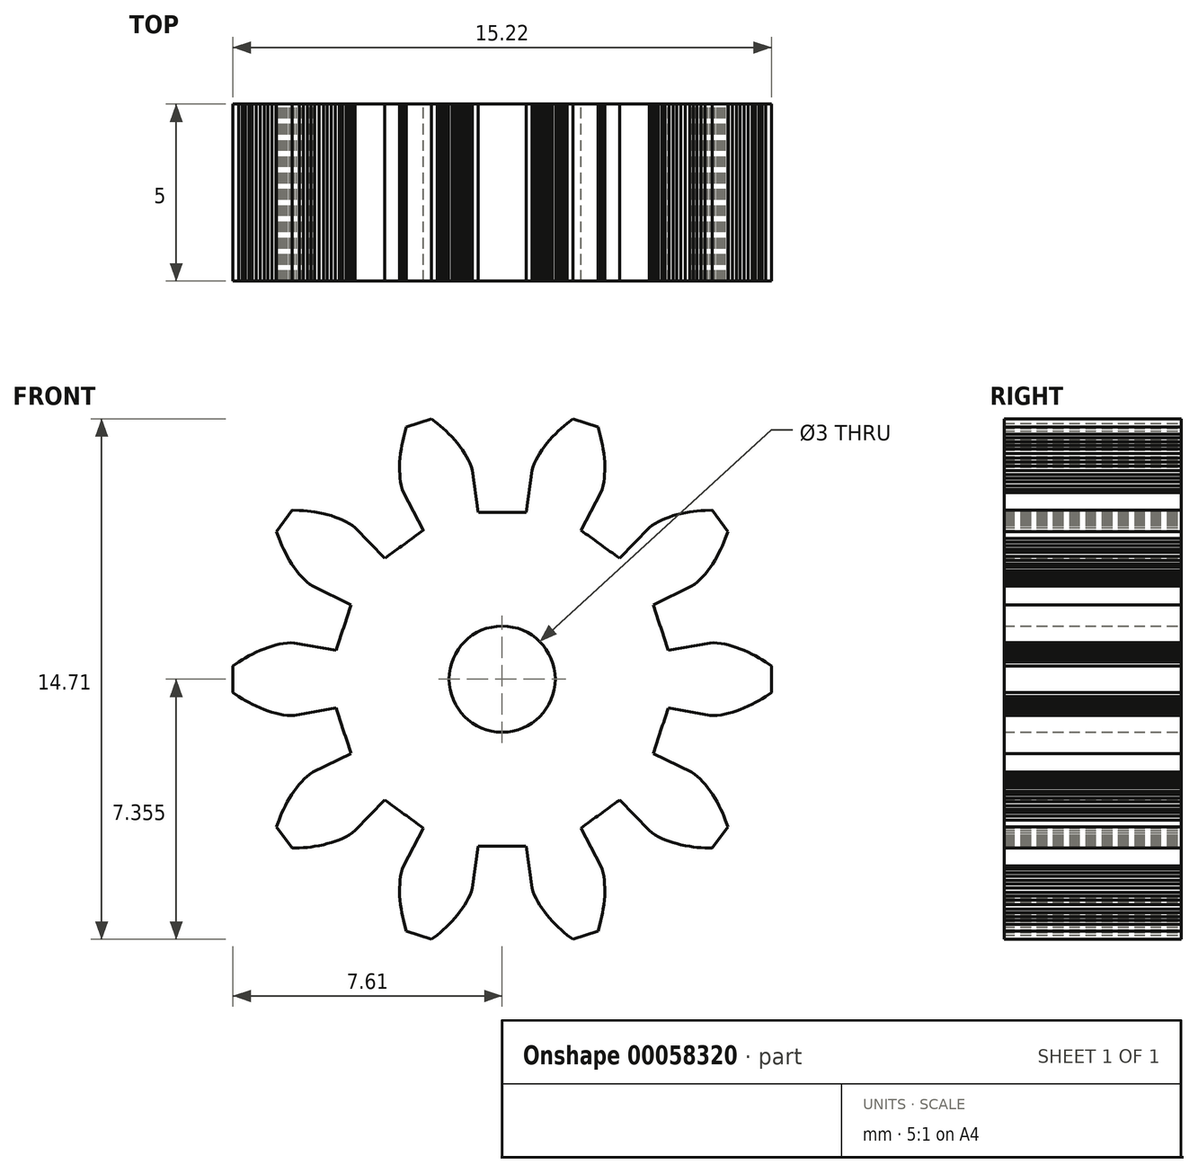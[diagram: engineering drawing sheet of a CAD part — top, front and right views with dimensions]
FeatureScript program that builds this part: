
annotation { "Feature Type Name" : "Feature", "Feature Type Description" : "" }
export const myFeature = defineFeature(function(context is Context, id is Id, definition is map)
    precondition{}
    {
        {
            var Q0;
            Q0=qCreatedBy(makeId("Front.planeOp"),FACE);
            var sketch = newSketch(context, id + "F0", { "sketchPlane" : qUnion([Q0])});
            skLineSegment(sketch, "E0", {"start": v(4.7, 0.36) * mm, "end": v(5.88, 0.15) * mm});
            skLineSegment(sketch, "E1", {"start": v(5.88, 0.15) * mm, "end": v(5.98, 0.15) * mm});
            skLineSegment(sketch, "E2", {"start": v(5.98, 0.15) * mm, "end": v(6.08, 0.15) * mm});
            skLineSegment(sketch, "E3", {"start": v(6.08, 0.15) * mm, "end": v(6.19, 0.17) * mm});
            skLineSegment(sketch, "E4", {"start": v(6.19, 0.17) * mm, "end": v(6.3, 0.19) * mm});
            skLineSegment(sketch, "E5", {"start": v(6.3, 0.19) * mm, "end": v(6.4, 0.2) * mm});
            skLineSegment(sketch, "E6", {"start": v(6.4, 0.2) * mm, "end": v(6.5, 0.24) * mm});
            skLineSegment(sketch, "E7", {"start": v(6.5, 0.24) * mm, "end": v(6.63, 0.28) * mm});
            skLineSegment(sketch, "E8", {"start": v(6.63, 0.28) * mm, "end": v(6.73, 0.32) * mm});
            skLineSegment(sketch, "E9", {"start": v(6.73, 0.32) * mm, "end": v(6.84, 0.36) * mm});
            skLineSegment(sketch, "E10", {"start": v(6.84, 0.36) * mm, "end": v(6.95, 0.4) * mm});
            skLineSegment(sketch, "E11", {"start": v(6.95, 0.4) * mm, "end": v(7.07, 0.47) * mm});
            skLineSegment(sketch, "E12", {"start": v(7.07, 0.47) * mm, "end": v(7.16, 0.52) * mm});
            skLineSegment(sketch, "E13", {"start": v(7.16, 0.52) * mm, "end": v(7.25, 0.57) * mm});
            skLineSegment(sketch, "E14", {"start": v(7.25, 0.57) * mm, "end": v(7.35, 0.63) * mm});
            skLineSegment(sketch, "E15", {"start": v(7.35, 0.63) * mm, "end": v(7.44, 0.69) * mm});
            skLineSegment(sketch, "E16", {"start": v(7.44, 0.69) * mm, "end": v(7.61, 0.8) * mm});
            skLineSegment(sketch, "E17", {"start": v(7.61, 0.8) * mm, "end": v(7.61, 1.55) * mm});
            skLineSegment(sketch, "E18", {"start": v(7.61, 1.55) * mm, "end": v(7.44, 1.66) * mm});
            skLineSegment(sketch, "E19", {"start": v(7.44, 1.66) * mm, "end": v(7.35, 1.72) * mm});
            skLineSegment(sketch, "E20", {"start": v(7.35, 1.72) * mm, "end": v(7.25, 1.78) * mm});
            skLineSegment(sketch, "E21", {"start": v(7.25, 1.78) * mm, "end": v(7.16, 1.83) * mm});
            skLineSegment(sketch, "E22", {"start": v(7.16, 1.83) * mm, "end": v(7.07, 1.88) * mm});
            skLineSegment(sketch, "E23", {"start": v(7.07, 1.88) * mm, "end": v(6.95, 1.94) * mm});
            skLineSegment(sketch, "E24", {"start": v(6.95, 1.94) * mm, "end": v(6.84, 1.99) * mm});
            skLineSegment(sketch, "E25", {"start": v(6.84, 1.99) * mm, "end": v(6.73, 2.03) * mm});
            skLineSegment(sketch, "E26", {"start": v(6.73, 2.03) * mm, "end": v(6.63, 2.07) * mm});
            skLineSegment(sketch, "E27", {"start": v(6.63, 2.07) * mm, "end": v(6.5, 2.1) * mm});
            skLineSegment(sketch, "E28", {"start": v(6.5, 2.1) * mm, "end": v(6.4, 2.14) * mm});
            skLineSegment(sketch, "E29", {"start": v(6.4, 2.14) * mm, "end": v(6.3, 2.16) * mm});
            skLineSegment(sketch, "E30", {"start": v(6.3, 2.16) * mm, "end": v(6.19, 2.18) * mm});
            skLineSegment(sketch, "E31", {"start": v(6.19, 2.18) * mm, "end": v(6.08, 2.2) * mm});
            skLineSegment(sketch, "E32", {"start": v(6.08, 2.2) * mm, "end": v(5.98, 2.2) * mm});
            skLineSegment(sketch, "E33", {"start": v(5.98, 2.2) * mm, "end": v(5.88, 2.2) * mm});
            skLineSegment(sketch, "E34", {"start": v(5.88, 2.2) * mm, "end": v(4.7, 1.99) * mm});
            skArc(sketch, "E35", {"start": v(4.7, 1.99) * mm, "mid": v(4.48, 2.63) * mm, "end": v(4.28, 3.27) * mm});
            skLineSegment(sketch, "E36", {"start": v(4.28, 3.27) * mm, "end": v(5.36, 3.8) * mm});
            skLineSegment(sketch, "E37", {"start": v(5.36, 3.8) * mm, "end": v(5.44, 3.86) * mm});
            skLineSegment(sketch, "E38", {"start": v(5.44, 3.86) * mm, "end": v(5.52, 3.92) * mm});
            skLineSegment(sketch, "E39", {"start": v(5.52, 3.92) * mm, "end": v(5.6, 4) * mm});
            skLineSegment(sketch, "E40", {"start": v(5.6, 4) * mm, "end": v(5.67, 4.08) * mm});
            skLineSegment(sketch, "E41", {"start": v(5.67, 4.08) * mm, "end": v(5.74, 4.15) * mm});
            skLineSegment(sketch, "E42", {"start": v(5.74, 4.15) * mm, "end": v(5.81, 4.24) * mm});
            skLineSegment(sketch, "E43", {"start": v(5.81, 4.24) * mm, "end": v(5.89, 4.34) * mm});
            skLineSegment(sketch, "E44", {"start": v(5.89, 4.34) * mm, "end": v(5.95, 4.44) * mm});
            skLineSegment(sketch, "E45", {"start": v(5.95, 4.44) * mm, "end": v(6.01, 4.53) * mm});
            skLineSegment(sketch, "E46", {"start": v(6.01, 4.53) * mm, "end": v(6.07, 4.64) * mm});
            skLineSegment(sketch, "E47", {"start": v(6.07, 4.64) * mm, "end": v(6.13, 4.76) * mm});
            skLineSegment(sketch, "E48", {"start": v(6.13, 4.76) * mm, "end": v(6.18, 4.85) * mm});
            skLineSegment(sketch, "E49", {"start": v(6.18, 4.85) * mm, "end": v(6.22, 4.95) * mm});
            skLineSegment(sketch, "E50", {"start": v(6.22, 4.95) * mm, "end": v(6.27, 5.05) * mm});
            skLineSegment(sketch, "E51", {"start": v(6.27, 5.05) * mm, "end": v(6.3, 5.16) * mm});
            skLineSegment(sketch, "E52", {"start": v(6.3, 5.16) * mm, "end": v(6.38, 5.35) * mm});
            skLineSegment(sketch, "E53", {"start": v(6.38, 5.35) * mm, "end": v(5.94, 5.95) * mm});
            skLineSegment(sketch, "E54", {"start": v(5.94, 5.95) * mm, "end": v(5.74, 5.94) * mm});
            skLineSegment(sketch, "E55", {"start": v(5.74, 5.94) * mm, "end": v(5.62, 5.94) * mm});
            skLineSegment(sketch, "E56", {"start": v(5.62, 5.94) * mm, "end": v(5.51, 5.93) * mm});
            skLineSegment(sketch, "E57", {"start": v(5.51, 5.93) * mm, "end": v(5.4, 5.92) * mm});
            skLineSegment(sketch, "E58", {"start": v(5.4, 5.92) * mm, "end": v(5.3, 5.9) * mm});
            skLineSegment(sketch, "E59", {"start": v(5.3, 5.9) * mm, "end": v(5.17, 5.88) * mm});
            skLineSegment(sketch, "E60", {"start": v(5.17, 5.88) * mm, "end": v(5.05, 5.85) * mm});
            skLineSegment(sketch, "E61", {"start": v(5.05, 5.85) * mm, "end": v(4.94, 5.83) * mm});
            skLineSegment(sketch, "E62", {"start": v(4.94, 5.83) * mm, "end": v(4.83, 5.8) * mm});
            skLineSegment(sketch, "E63", {"start": v(4.83, 5.8) * mm, "end": v(4.71, 5.76) * mm});
            skLineSegment(sketch, "E64", {"start": v(4.71, 5.76) * mm, "end": v(4.6, 5.72) * mm});
            skLineSegment(sketch, "E65", {"start": v(4.6, 5.72) * mm, "end": v(4.51, 5.68) * mm});
            skLineSegment(sketch, "E66", {"start": v(4.51, 5.68) * mm, "end": v(4.41, 5.63) * mm});
            skLineSegment(sketch, "E67", {"start": v(4.41, 5.63) * mm, "end": v(4.32, 5.58) * mm});
            skLineSegment(sketch, "E68", {"start": v(4.32, 5.58) * mm, "end": v(4.23, 5.52) * mm});
            skLineSegment(sketch, "E69", {"start": v(4.23, 5.52) * mm, "end": v(4.16, 5.46) * mm});
            skLineSegment(sketch, "E70", {"start": v(4.16, 5.46) * mm, "end": v(3.32, 4.6) * mm});
            skArc(sketch, "E71", {"start": v(3.32, 4.6) * mm, "mid": v(2.77, 4.99) * mm, "end": v(2.23, 5.39) * mm});
            skLineSegment(sketch, "E72", {"start": v(2.23, 5.39) * mm, "end": v(2.79, 6.45) * mm});
            skLineSegment(sketch, "E73", {"start": v(2.79, 6.45) * mm, "end": v(2.82, 6.54) * mm});
            skLineSegment(sketch, "E74", {"start": v(2.82, 6.54) * mm, "end": v(2.85, 6.64) * mm});
            skLineSegment(sketch, "E75", {"start": v(2.85, 6.64) * mm, "end": v(2.87, 6.75) * mm});
            skLineSegment(sketch, "E76", {"start": v(2.87, 6.75) * mm, "end": v(2.89, 6.86) * mm});
            skLineSegment(sketch, "E77", {"start": v(2.89, 6.86) * mm, "end": v(2.9, 6.96) * mm});
            skLineSegment(sketch, "E78", {"start": v(2.9, 6.96) * mm, "end": v(2.9, 7.07) * mm});
            skLineSegment(sketch, "E79", {"start": v(2.9, 7.07) * mm, "end": v(2.9, 7.2) * mm});
            skLineSegment(sketch, "E80", {"start": v(2.9, 7.2) * mm, "end": v(2.9, 7.3) * mm});
            skLineSegment(sketch, "E81", {"start": v(2.9, 7.3) * mm, "end": v(2.89, 7.43) * mm});
            skLineSegment(sketch, "E82", {"start": v(2.89, 7.43) * mm, "end": v(2.87, 7.55) * mm});
            skLineSegment(sketch, "E83", {"start": v(2.87, 7.55) * mm, "end": v(2.86, 7.68) * mm});
            skLineSegment(sketch, "E84", {"start": v(2.86, 7.68) * mm, "end": v(2.84, 7.78) * mm});
            skLineSegment(sketch, "E85", {"start": v(2.84, 7.78) * mm, "end": v(2.82, 7.88) * mm});
            skLineSegment(sketch, "E86", {"start": v(2.82, 7.88) * mm, "end": v(2.8, 8) * mm});
            skLineSegment(sketch, "E87", {"start": v(2.8, 8) * mm, "end": v(2.76, 8.1) * mm});
            skLineSegment(sketch, "E88", {"start": v(2.76, 8.1) * mm, "end": v(2.7, 8.3) * mm});
            skLineSegment(sketch, "E89", {"start": v(2.7, 8.3) * mm, "end": v(2, 8.53) * mm});
            skLineSegment(sketch, "E90", {"start": v(2, 8.53) * mm, "end": v(1.84, 8.4) * mm});
            skLineSegment(sketch, "E91", {"start": v(1.84, 8.4) * mm, "end": v(1.75, 8.33) * mm});
            skLineSegment(sketch, "E92", {"start": v(1.75, 8.33) * mm, "end": v(1.66, 8.26) * mm});
            skLineSegment(sketch, "E93", {"start": v(1.66, 8.26) * mm, "end": v(1.59, 8.19) * mm});
            skLineSegment(sketch, "E94", {"start": v(1.59, 8.19) * mm, "end": v(1.51, 8.11) * mm});
            skLineSegment(sketch, "E95", {"start": v(1.51, 8.11) * mm, "end": v(1.42, 8.02) * mm});
            skLineSegment(sketch, "E96", {"start": v(1.42, 8.02) * mm, "end": v(1.34, 7.93) * mm});
            skLineSegment(sketch, "E97", {"start": v(1.34, 7.93) * mm, "end": v(1.26, 7.84) * mm});
            skLineSegment(sketch, "E98", {"start": v(1.26, 7.84) * mm, "end": v(1.2, 7.75) * mm});
            skLineSegment(sketch, "E99", {"start": v(1.2, 7.75) * mm, "end": v(1.12, 7.65) * mm});
            skLineSegment(sketch, "E100", {"start": v(1.12, 7.65) * mm, "end": v(1.06, 7.56) * mm});
            skLineSegment(sketch, "E101", {"start": v(1.06, 7.56) * mm, "end": v(1, 7.47) * mm});
            skLineSegment(sketch, "E102", {"start": v(1, 7.47) * mm, "end": v(0.95, 7.37) * mm});
            skLineSegment(sketch, "E103", {"start": v(0.95, 7.37) * mm, "end": v(0.9, 7.28) * mm});
            skLineSegment(sketch, "E104", {"start": v(0.9, 7.28) * mm, "end": v(0.87, 7.18) * mm});
            skLineSegment(sketch, "E105", {"start": v(0.87, 7.18) * mm, "end": v(0.85, 7.08) * mm});
            skLineSegment(sketch, "E106", {"start": v(0.85, 7.08) * mm, "end": v(0.67, 5.89) * mm});
            skArc(sketch, "E107", {"start": v(0.67, 5.89) * mm, "mid": v(0, 5.89) * mm, "end": v(-0.67, 5.89) * mm});
            skLineSegment(sketch, "E108", {"start": v(-0.67, 5.89) * mm, "end": v(-0.85, 7.08) * mm});
            skLineSegment(sketch, "E109", {"start": v(-0.85, 7.08) * mm, "end": v(-0.87, 7.18) * mm});
            skLineSegment(sketch, "E110", {"start": v(-0.87, 7.18) * mm, "end": v(-0.9, 7.28) * mm});
            skLineSegment(sketch, "E111", {"start": v(-0.9, 7.28) * mm, "end": v(-0.95, 7.37) * mm});
            skLineSegment(sketch, "E112", {"start": v(-0.95, 7.37) * mm, "end": v(-1, 7.47) * mm});
            skLineSegment(sketch, "E113", {"start": v(-1, 7.47) * mm, "end": v(-1.06, 7.56) * mm});
            skLineSegment(sketch, "E114", {"start": v(-1.06, 7.56) * mm, "end": v(-1.12, 7.65) * mm});
            skLineSegment(sketch, "E115", {"start": v(-1.12, 7.65) * mm, "end": v(-1.2, 7.75) * mm});
            skLineSegment(sketch, "E116", {"start": v(-1.2, 7.75) * mm, "end": v(-1.26, 7.84) * mm});
            skLineSegment(sketch, "E117", {"start": v(-1.26, 7.84) * mm, "end": v(-1.34, 7.93) * mm});
            skLineSegment(sketch, "E118", {"start": v(-1.34, 7.93) * mm, "end": v(-1.42, 8.02) * mm});
            skLineSegment(sketch, "E119", {"start": v(-1.42, 8.02) * mm, "end": v(-1.51, 8.11) * mm});
            skLineSegment(sketch, "E120", {"start": v(-1.51, 8.11) * mm, "end": v(-1.59, 8.19) * mm});
            skLineSegment(sketch, "E121", {"start": v(-1.59, 8.19) * mm, "end": v(-1.66, 8.26) * mm});
            skLineSegment(sketch, "E122", {"start": v(-1.66, 8.26) * mm, "end": v(-1.75, 8.33) * mm});
            skLineSegment(sketch, "E123", {"start": v(-1.75, 8.33) * mm, "end": v(-1.84, 8.4) * mm});
            skLineSegment(sketch, "E124", {"start": v(-1.84, 8.4) * mm, "end": v(-2, 8.53) * mm});
            skLineSegment(sketch, "E125", {"start": v(-2, 8.53) * mm, "end": v(-2.7, 8.3) * mm});
            skLineSegment(sketch, "E126", {"start": v(-2.7, 8.3) * mm, "end": v(-2.76, 8.1) * mm});
            skLineSegment(sketch, "E127", {"start": v(-2.76, 8.1) * mm, "end": v(-2.8, 8) * mm});
            skLineSegment(sketch, "E128", {"start": v(-2.8, 8) * mm, "end": v(-2.82, 7.88) * mm});
            skLineSegment(sketch, "E129", {"start": v(-2.82, 7.88) * mm, "end": v(-2.84, 7.78) * mm});
            skLineSegment(sketch, "E130", {"start": v(-2.84, 7.78) * mm, "end": v(-2.86, 7.68) * mm});
            skLineSegment(sketch, "E131", {"start": v(-2.86, 7.68) * mm, "end": v(-2.87, 7.55) * mm});
            skLineSegment(sketch, "E132", {"start": v(-2.87, 7.55) * mm, "end": v(-2.89, 7.43) * mm});
            skLineSegment(sketch, "E133", {"start": v(-2.89, 7.43) * mm, "end": v(-2.9, 7.3) * mm});
            skLineSegment(sketch, "E134", {"start": v(-2.9, 7.3) * mm, "end": v(-2.9, 7.2) * mm});
            skLineSegment(sketch, "E135", {"start": v(-2.9, 7.2) * mm, "end": v(-2.9, 7.07) * mm});
            skLineSegment(sketch, "E136", {"start": v(-2.9, 7.07) * mm, "end": v(-2.9, 6.96) * mm});
            skLineSegment(sketch, "E137", {"start": v(-2.9, 6.96) * mm, "end": v(-2.89, 6.86) * mm});
            skLineSegment(sketch, "E138", {"start": v(-2.89, 6.86) * mm, "end": v(-2.87, 6.75) * mm});
            skLineSegment(sketch, "E139", {"start": v(-2.87, 6.75) * mm, "end": v(-2.85, 6.64) * mm});
            skLineSegment(sketch, "E140", {"start": v(-2.85, 6.64) * mm, "end": v(-2.82, 6.54) * mm});
            skLineSegment(sketch, "E141", {"start": v(-2.82, 6.54) * mm, "end": v(-2.79, 6.45) * mm});
            skLineSegment(sketch, "E142", {"start": v(-2.79, 6.45) * mm, "end": v(-2.23, 5.39) * mm});
            skArc(sketch, "E143", {"start": v(-2.23, 5.39) * mm, "mid": v(-2.77, 4.99) * mm, "end": v(-3.32, 4.6) * mm});
            skLineSegment(sketch, "E144", {"start": v(-3.32, 4.6) * mm, "end": v(-4.16, 5.46) * mm});
            skLineSegment(sketch, "E145", {"start": v(-4.16, 5.46) * mm, "end": v(-4.23, 5.52) * mm});
            skLineSegment(sketch, "E146", {"start": v(-4.23, 5.52) * mm, "end": v(-4.32, 5.58) * mm});
            skLineSegment(sketch, "E147", {"start": v(-4.32, 5.58) * mm, "end": v(-4.41, 5.63) * mm});
            skLineSegment(sketch, "E148", {"start": v(-4.41, 5.63) * mm, "end": v(-4.51, 5.68) * mm});
            skLineSegment(sketch, "E149", {"start": v(-4.51, 5.68) * mm, "end": v(-4.6, 5.72) * mm});
            skLineSegment(sketch, "E150", {"start": v(-4.6, 5.72) * mm, "end": v(-4.71, 5.76) * mm});
            skLineSegment(sketch, "E151", {"start": v(-4.71, 5.76) * mm, "end": v(-4.83, 5.8) * mm});
            skLineSegment(sketch, "E152", {"start": v(-4.83, 5.8) * mm, "end": v(-4.94, 5.83) * mm});
            skLineSegment(sketch, "E153", {"start": v(-4.94, 5.83) * mm, "end": v(-5.05, 5.85) * mm});
            skLineSegment(sketch, "E154", {"start": v(-5.05, 5.85) * mm, "end": v(-5.17, 5.88) * mm});
            skLineSegment(sketch, "E155", {"start": v(-5.17, 5.88) * mm, "end": v(-5.3, 5.9) * mm});
            skLineSegment(sketch, "E156", {"start": v(-5.3, 5.9) * mm, "end": v(-5.4, 5.92) * mm});
            skLineSegment(sketch, "E157", {"start": v(-5.4, 5.92) * mm, "end": v(-5.51, 5.93) * mm});
            skLineSegment(sketch, "E158", {"start": v(-5.51, 5.93) * mm, "end": v(-5.62, 5.94) * mm});
            skLineSegment(sketch, "E159", {"start": v(-5.62, 5.94) * mm, "end": v(-5.74, 5.94) * mm});
            skLineSegment(sketch, "E160", {"start": v(-5.74, 5.94) * mm, "end": v(-5.94, 5.95) * mm});
            skLineSegment(sketch, "E161", {"start": v(-5.94, 5.95) * mm, "end": v(-6.38, 5.35) * mm});
            skLineSegment(sketch, "E162", {"start": v(-6.38, 5.35) * mm, "end": v(-6.3, 5.16) * mm});
            skLineSegment(sketch, "E163", {"start": v(-6.3, 5.16) * mm, "end": v(-6.27, 5.05) * mm});
            skLineSegment(sketch, "E164", {"start": v(-6.27, 5.05) * mm, "end": v(-6.22, 4.95) * mm});
            skLineSegment(sketch, "E165", {"start": v(-6.22, 4.95) * mm, "end": v(-6.18, 4.85) * mm});
            skLineSegment(sketch, "E166", {"start": v(-6.18, 4.85) * mm, "end": v(-6.13, 4.76) * mm});
            skLineSegment(sketch, "E167", {"start": v(-6.13, 4.76) * mm, "end": v(-6.07, 4.64) * mm});
            skLineSegment(sketch, "E168", {"start": v(-6.07, 4.64) * mm, "end": v(-6.01, 4.53) * mm});
            skLineSegment(sketch, "E169", {"start": v(-6.01, 4.53) * mm, "end": v(-5.95, 4.44) * mm});
            skLineSegment(sketch, "E170", {"start": v(-5.95, 4.44) * mm, "end": v(-5.89, 4.34) * mm});
            skLineSegment(sketch, "E171", {"start": v(-5.89, 4.34) * mm, "end": v(-5.81, 4.24) * mm});
            skLineSegment(sketch, "E172", {"start": v(-5.81, 4.24) * mm, "end": v(-5.74, 4.15) * mm});
            skLineSegment(sketch, "E173", {"start": v(-5.74, 4.15) * mm, "end": v(-5.67, 4.08) * mm});
            skLineSegment(sketch, "E174", {"start": v(-5.67, 4.08) * mm, "end": v(-5.6, 4) * mm});
            skLineSegment(sketch, "E175", {"start": v(-5.6, 4) * mm, "end": v(-5.52, 3.92) * mm});
            skLineSegment(sketch, "E176", {"start": v(-5.52, 3.92) * mm, "end": v(-5.44, 3.86) * mm});
            skLineSegment(sketch, "E177", {"start": v(-5.44, 3.86) * mm, "end": v(-5.36, 3.8) * mm});
            skLineSegment(sketch, "E178", {"start": v(-5.36, 3.8) * mm, "end": v(-4.28, 3.27) * mm});
            skArc(sketch, "E179", {"start": v(-4.28, 3.27) * mm, "mid": v(-4.48, 2.63) * mm, "end": v(-4.7, 1.99) * mm});
            skLineSegment(sketch, "E180", {"start": v(-4.7, 1.99) * mm, "end": v(-5.88, 2.2) * mm});
            skLineSegment(sketch, "E181", {"start": v(-5.88, 2.2) * mm, "end": v(-5.98, 2.2) * mm});
            skLineSegment(sketch, "E182", {"start": v(-5.98, 2.2) * mm, "end": v(-6.08, 2.2) * mm});
            skLineSegment(sketch, "E183", {"start": v(-6.08, 2.2) * mm, "end": v(-6.19, 2.18) * mm});
            skLineSegment(sketch, "E184", {"start": v(-6.19, 2.18) * mm, "end": v(-6.3, 2.16) * mm});
            skLineSegment(sketch, "E185", {"start": v(-6.3, 2.16) * mm, "end": v(-6.4, 2.14) * mm});
            skLineSegment(sketch, "E186", {"start": v(-6.4, 2.14) * mm, "end": v(-6.5, 2.1) * mm});
            skLineSegment(sketch, "E187", {"start": v(-6.5, 2.1) * mm, "end": v(-6.63, 2.07) * mm});
            skLineSegment(sketch, "E188", {"start": v(-6.63, 2.07) * mm, "end": v(-6.73, 2.03) * mm});
            skLineSegment(sketch, "E189", {"start": v(-6.73, 2.03) * mm, "end": v(-6.84, 1.99) * mm});
            skLineSegment(sketch, "E190", {"start": v(-6.84, 1.99) * mm, "end": v(-6.95, 1.94) * mm});
            skLineSegment(sketch, "E191", {"start": v(-6.95, 1.94) * mm, "end": v(-7.07, 1.88) * mm});
            skLineSegment(sketch, "E192", {"start": v(-7.07, 1.88) * mm, "end": v(-7.16, 1.83) * mm});
            skLineSegment(sketch, "E193", {"start": v(-7.16, 1.83) * mm, "end": v(-7.25, 1.78) * mm});
            skLineSegment(sketch, "E194", {"start": v(-7.25, 1.78) * mm, "end": v(-7.35, 1.72) * mm});
            skLineSegment(sketch, "E195", {"start": v(-7.35, 1.72) * mm, "end": v(-7.44, 1.66) * mm});
            skLineSegment(sketch, "E196", {"start": v(-7.44, 1.66) * mm, "end": v(-7.61, 1.55) * mm});
            skLineSegment(sketch, "E197", {"start": v(-7.61, 1.55) * mm, "end": v(-7.61, 0.8) * mm});
            skLineSegment(sketch, "E198", {"start": v(-7.61, 0.8) * mm, "end": v(-7.44, 0.69) * mm});
            skLineSegment(sketch, "E199", {"start": v(-7.44, 0.69) * mm, "end": v(-7.35, 0.63) * mm});
            skLineSegment(sketch, "E200", {"start": v(-7.35, 0.63) * mm, "end": v(-7.25, 0.57) * mm});
            skLineSegment(sketch, "E201", {"start": v(-7.25, 0.57) * mm, "end": v(-7.16, 0.52) * mm});
            skLineSegment(sketch, "E202", {"start": v(-7.16, 0.52) * mm, "end": v(-7.07, 0.47) * mm});
            skLineSegment(sketch, "E203", {"start": v(-7.07, 0.47) * mm, "end": v(-6.95, 0.4) * mm});
            skLineSegment(sketch, "E204", {"start": v(-6.95, 0.4) * mm, "end": v(-6.84, 0.36) * mm});
            skLineSegment(sketch, "E205", {"start": v(-6.84, 0.36) * mm, "end": v(-6.73, 0.32) * mm});
            skLineSegment(sketch, "E206", {"start": v(-6.73, 0.32) * mm, "end": v(-6.63, 0.28) * mm});
            skLineSegment(sketch, "E207", {"start": v(-6.63, 0.28) * mm, "end": v(-6.5, 0.24) * mm});
            skLineSegment(sketch, "E208", {"start": v(-6.5, 0.24) * mm, "end": v(-6.4, 0.2) * mm});
            skLineSegment(sketch, "E209", {"start": v(-6.4, 0.2) * mm, "end": v(-6.3, 0.19) * mm});
            skLineSegment(sketch, "E210", {"start": v(-6.3, 0.19) * mm, "end": v(-6.19, 0.17) * mm});
            skLineSegment(sketch, "E211", {"start": v(-6.19, 0.17) * mm, "end": v(-6.08, 0.15) * mm});
            skLineSegment(sketch, "E212", {"start": v(-6.08, 0.15) * mm, "end": v(-5.98, 0.15) * mm});
            skLineSegment(sketch, "E213", {"start": v(-5.98, 0.15) * mm, "end": v(-5.88, 0.15) * mm});
            skLineSegment(sketch, "E214", {"start": v(-5.88, 0.15) * mm, "end": v(-4.7, 0.36) * mm});
            skArc(sketch, "E215", {"start": v(-4.7, 0.36) * mm, "mid": v(-4.48, -0.28) * mm, "end": v(-4.28, -0.92) * mm});
            skLineSegment(sketch, "E216", {"start": v(-4.28, -0.92) * mm, "end": v(-5.36, -1.45) * mm});
            skLineSegment(sketch, "E217", {"start": v(-5.36, -1.45) * mm, "end": v(-5.44, -1.5) * mm});
            skLineSegment(sketch, "E218", {"start": v(-5.44, -1.5) * mm, "end": v(-5.52, -1.57) * mm});
            skLineSegment(sketch, "E219", {"start": v(-5.52, -1.57) * mm, "end": v(-5.6, -1.65) * mm});
            skLineSegment(sketch, "E220", {"start": v(-5.6, -1.65) * mm, "end": v(-5.67, -1.73) * mm});
            skLineSegment(sketch, "E221", {"start": v(-5.67, -1.73) * mm, "end": v(-5.74, -1.8) * mm});
            skLineSegment(sketch, "E222", {"start": v(-5.74, -1.8) * mm, "end": v(-5.81, -1.9) * mm});
            skLineSegment(sketch, "E223", {"start": v(-5.81, -1.9) * mm, "end": v(-5.89, -2) * mm});
            skLineSegment(sketch, "E224", {"start": v(-5.89, -2) * mm, "end": v(-5.95, -2.09) * mm});
            skLineSegment(sketch, "E225", {"start": v(-5.95, -2.09) * mm, "end": v(-6.01, -2.18) * mm});
            skLineSegment(sketch, "E226", {"start": v(-6.01, -2.18) * mm, "end": v(-6.07, -2.3) * mm});
            skLineSegment(sketch, "E227", {"start": v(-6.07, -2.3) * mm, "end": v(-6.13, -2.4) * mm});
            skLineSegment(sketch, "E228", {"start": v(-6.13, -2.4) * mm, "end": v(-6.18, -2.5) * mm});
            skLineSegment(sketch, "E229", {"start": v(-6.18, -2.5) * mm, "end": v(-6.22, -2.6) * mm});
            skLineSegment(sketch, "E230", {"start": v(-6.22, -2.6) * mm, "end": v(-6.27, -2.7) * mm});
            skLineSegment(sketch, "E231", {"start": v(-6.27, -2.7) * mm, "end": v(-6.3, -2.8) * mm});
            skLineSegment(sketch, "E232", {"start": v(-6.3, -2.8) * mm, "end": v(-6.38, -3) * mm});
            skLineSegment(sketch, "E233", {"start": v(-6.38, -3) * mm, "end": v(-5.94, -3.6) * mm});
            skLineSegment(sketch, "E234", {"start": v(-5.94, -3.6) * mm, "end": v(-5.74, -3.6) * mm});
            skLineSegment(sketch, "E235", {"start": v(-5.74, -3.6) * mm, "end": v(-5.62, -3.59) * mm});
            skLineSegment(sketch, "E236", {"start": v(-5.62, -3.59) * mm, "end": v(-5.51, -3.58) * mm});
            skLineSegment(sketch, "E237", {"start": v(-5.51, -3.58) * mm, "end": v(-5.4, -3.57) * mm});
            skLineSegment(sketch, "E238", {"start": v(-5.4, -3.57) * mm, "end": v(-5.3, -3.55) * mm});
            skLineSegment(sketch, "E239", {"start": v(-5.3, -3.55) * mm, "end": v(-5.17, -3.53) * mm});
            skLineSegment(sketch, "E240", {"start": v(-5.17, -3.53) * mm, "end": v(-5.05, -3.5) * mm});
            skLineSegment(sketch, "E241", {"start": v(-5.05, -3.5) * mm, "end": v(-4.94, -3.48) * mm});
            skLineSegment(sketch, "E242", {"start": v(-4.94, -3.48) * mm, "end": v(-4.83, -3.45) * mm});
            skLineSegment(sketch, "E243", {"start": v(-4.83, -3.45) * mm, "end": v(-4.71, -3.4) * mm});
            skLineSegment(sketch, "E244", {"start": v(-4.71, -3.4) * mm, "end": v(-4.6, -3.37) * mm});
            skLineSegment(sketch, "E245", {"start": v(-4.6, -3.37) * mm, "end": v(-4.51, -3.33) * mm});
            skLineSegment(sketch, "E246", {"start": v(-4.51, -3.33) * mm, "end": v(-4.41, -3.28) * mm});
            skLineSegment(sketch, "E247", {"start": v(-4.41, -3.28) * mm, "end": v(-4.32, -3.23) * mm});
            skLineSegment(sketch, "E248", {"start": v(-4.32, -3.23) * mm, "end": v(-4.23, -3.17) * mm});
            skLineSegment(sketch, "E249", {"start": v(-4.23, -3.17) * mm, "end": v(-4.16, -3.1) * mm});
            skLineSegment(sketch, "E250", {"start": v(-4.16, -3.1) * mm, "end": v(-3.32, -2.24) * mm});
            skArc(sketch, "E251", {"start": v(-3.32, -2.24) * mm, "mid": v(-2.77, -2.64) * mm, "end": v(-2.23, -3.04) * mm});
            skLineSegment(sketch, "E252", {"start": v(-2.23, -3.04) * mm, "end": v(-2.79, -4.1) * mm});
            skLineSegment(sketch, "E253", {"start": v(-2.79, -4.1) * mm, "end": v(-2.82, -4.2) * mm});
            skLineSegment(sketch, "E254", {"start": v(-2.82, -4.2) * mm, "end": v(-2.85, -4.3) * mm});
            skLineSegment(sketch, "E255", {"start": v(-2.85, -4.3) * mm, "end": v(-2.87, -4.4) * mm});
            skLineSegment(sketch, "E256", {"start": v(-2.87, -4.4) * mm, "end": v(-2.89, -4.5) * mm});
            skLineSegment(sketch, "E257", {"start": v(-2.89, -4.5) * mm, "end": v(-2.9, -4.61) * mm});
            skLineSegment(sketch, "E258", {"start": v(-2.9, -4.61) * mm, "end": v(-2.9, -4.73) * mm});
            skLineSegment(sketch, "E259", {"start": v(-2.9, -4.73) * mm, "end": v(-2.9, -4.85) * mm});
            skLineSegment(sketch, "E260", {"start": v(-2.9, -4.85) * mm, "end": v(-2.9, -4.96) * mm});
            skLineSegment(sketch, "E261", {"start": v(-2.9, -4.96) * mm, "end": v(-2.89, -5.08) * mm});
            skLineSegment(sketch, "E262", {"start": v(-2.89, -5.08) * mm, "end": v(-2.87, -5.2) * mm});
            skLineSegment(sketch, "E263", {"start": v(-2.87, -5.2) * mm, "end": v(-2.86, -5.33) * mm});
            skLineSegment(sketch, "E264", {"start": v(-2.86, -5.33) * mm, "end": v(-2.84, -5.43) * mm});
            skLineSegment(sketch, "E265", {"start": v(-2.84, -5.43) * mm, "end": v(-2.82, -5.54) * mm});
            skLineSegment(sketch, "E266", {"start": v(-2.82, -5.54) * mm, "end": v(-2.8, -5.64) * mm});
            skLineSegment(sketch, "E267", {"start": v(-2.8, -5.64) * mm, "end": v(-2.76, -5.76) * mm});
            skLineSegment(sketch, "E268", {"start": v(-2.76, -5.76) * mm, "end": v(-2.7, -5.95) * mm});
            skLineSegment(sketch, "E269", {"start": v(-2.7, -5.95) * mm, "end": v(-2, -6.18) * mm});
            skLineSegment(sketch, "E270", {"start": v(-2, -6.18) * mm, "end": v(-1.84, -6.06) * mm});
            skLineSegment(sketch, "E271", {"start": v(-1.84, -6.06) * mm, "end": v(-1.75, -5.98) * mm});
            skLineSegment(sketch, "E272", {"start": v(-1.75, -5.98) * mm, "end": v(-1.66, -5.9) * mm});
            skLineSegment(sketch, "E273", {"start": v(-1.66, -5.9) * mm, "end": v(-1.59, -5.84) * mm});
            skLineSegment(sketch, "E274", {"start": v(-1.59, -5.84) * mm, "end": v(-1.51, -5.77) * mm});
            skLineSegment(sketch, "E275", {"start": v(-1.51, -5.77) * mm, "end": v(-1.42, -5.67) * mm});
            skLineSegment(sketch, "E276", {"start": v(-1.42, -5.67) * mm, "end": v(-1.34, -5.58) * mm});
            skLineSegment(sketch, "E277", {"start": v(-1.34, -5.58) * mm, "end": v(-1.26, -5.5) * mm});
            skLineSegment(sketch, "E278", {"start": v(-1.26, -5.5) * mm, "end": v(-1.2, -5.4) * mm});
            skLineSegment(sketch, "E279", {"start": v(-1.2, -5.4) * mm, "end": v(-1.12, -5.3) * mm});
            skLineSegment(sketch, "E280", {"start": v(-1.12, -5.3) * mm, "end": v(-1.06, -5.2) * mm});
            skLineSegment(sketch, "E281", {"start": v(-1.06, -5.2) * mm, "end": v(-1, -5.12) * mm});
            skLineSegment(sketch, "E282", {"start": v(-1, -5.12) * mm, "end": v(-0.95, -5.02) * mm});
            skLineSegment(sketch, "E283", {"start": v(-0.95, -5.02) * mm, "end": v(-0.9, -4.93) * mm});
            skLineSegment(sketch, "E284", {"start": v(-0.9, -4.93) * mm, "end": v(-0.87, -4.83) * mm});
            skLineSegment(sketch, "E285", {"start": v(-0.87, -4.83) * mm, "end": v(-0.85, -4.73) * mm});
            skLineSegment(sketch, "E286", {"start": v(-0.85, -4.73) * mm, "end": v(-0.67, -3.54) * mm});
            skArc(sketch, "E287", {"start": v(-0.67, -3.54) * mm, "mid": v(0, -3.54) * mm, "end": v(0.67, -3.54) * mm});
            skLineSegment(sketch, "E288", {"start": v(0.67, -3.54) * mm, "end": v(0.85, -4.73) * mm});
            skLineSegment(sketch, "E289", {"start": v(0.85, -4.73) * mm, "end": v(0.87, -4.83) * mm});
            skLineSegment(sketch, "E290", {"start": v(0.87, -4.83) * mm, "end": v(0.9, -4.93) * mm});
            skLineSegment(sketch, "E291", {"start": v(0.9, -4.93) * mm, "end": v(0.95, -5.02) * mm});
            skLineSegment(sketch, "E292", {"start": v(0.95, -5.02) * mm, "end": v(1, -5.12) * mm});
            skLineSegment(sketch, "E293", {"start": v(1, -5.12) * mm, "end": v(1.06, -5.2) * mm});
            skLineSegment(sketch, "E294", {"start": v(1.06, -5.2) * mm, "end": v(1.12, -5.3) * mm});
            skLineSegment(sketch, "E295", {"start": v(1.12, -5.3) * mm, "end": v(1.2, -5.4) * mm});
            skLineSegment(sketch, "E296", {"start": v(1.2, -5.4) * mm, "end": v(1.26, -5.5) * mm});
            skLineSegment(sketch, "E297", {"start": v(1.26, -5.5) * mm, "end": v(1.34, -5.58) * mm});
            skLineSegment(sketch, "E298", {"start": v(1.34, -5.58) * mm, "end": v(1.42, -5.67) * mm});
            skLineSegment(sketch, "E299", {"start": v(1.42, -5.67) * mm, "end": v(1.51, -5.77) * mm});
            skLineSegment(sketch, "E300", {"start": v(1.51, -5.77) * mm, "end": v(1.59, -5.84) * mm});
            skLineSegment(sketch, "E301", {"start": v(1.59, -5.84) * mm, "end": v(1.66, -5.9) * mm});
            skLineSegment(sketch, "E302", {"start": v(1.66, -5.9) * mm, "end": v(1.75, -5.98) * mm});
            skLineSegment(sketch, "E303", {"start": v(1.75, -5.98) * mm, "end": v(1.84, -6.06) * mm});
            skLineSegment(sketch, "E304", {"start": v(1.84, -6.06) * mm, "end": v(2, -6.18) * mm});
            skLineSegment(sketch, "E305", {"start": v(2, -6.18) * mm, "end": v(2.7, -5.95) * mm});
            skLineSegment(sketch, "E306", {"start": v(2.7, -5.95) * mm, "end": v(2.76, -5.76) * mm});
            skLineSegment(sketch, "E307", {"start": v(2.76, -5.76) * mm, "end": v(2.8, -5.64) * mm});
            skLineSegment(sketch, "E308", {"start": v(2.8, -5.64) * mm, "end": v(2.82, -5.54) * mm});
            skLineSegment(sketch, "E309", {"start": v(2.82, -5.54) * mm, "end": v(2.84, -5.43) * mm});
            skLineSegment(sketch, "E310", {"start": v(2.84, -5.43) * mm, "end": v(2.86, -5.33) * mm});
            skLineSegment(sketch, "E311", {"start": v(2.86, -5.33) * mm, "end": v(2.87, -5.2) * mm});
            skLineSegment(sketch, "E312", {"start": v(2.87, -5.2) * mm, "end": v(2.89, -5.08) * mm});
            skLineSegment(sketch, "E313", {"start": v(2.89, -5.08) * mm, "end": v(2.9, -4.96) * mm});
            skLineSegment(sketch, "E314", {"start": v(2.9, -4.96) * mm, "end": v(2.9, -4.85) * mm});
            skLineSegment(sketch, "E315", {"start": v(2.9, -4.85) * mm, "end": v(2.9, -4.73) * mm});
            skLineSegment(sketch, "E316", {"start": v(2.9, -4.73) * mm, "end": v(2.9, -4.61) * mm});
            skLineSegment(sketch, "E317", {"start": v(2.9, -4.61) * mm, "end": v(2.89, -4.5) * mm});
            skLineSegment(sketch, "E318", {"start": v(2.89, -4.5) * mm, "end": v(2.87, -4.4) * mm});
            skLineSegment(sketch, "E319", {"start": v(2.87, -4.4) * mm, "end": v(2.85, -4.3) * mm});
            skLineSegment(sketch, "E320", {"start": v(2.85, -4.3) * mm, "end": v(2.82, -4.2) * mm});
            skLineSegment(sketch, "E321", {"start": v(2.82, -4.2) * mm, "end": v(2.79, -4.1) * mm});
            skLineSegment(sketch, "E322", {"start": v(2.79, -4.1) * mm, "end": v(2.23, -3.04) * mm});
            skArc(sketch, "E323", {"start": v(2.23, -3.04) * mm, "mid": v(2.77, -2.64) * mm, "end": v(3.32, -2.24) * mm});
            skLineSegment(sketch, "E324", {"start": v(3.32, -2.24) * mm, "end": v(4.16, -3.1) * mm});
            skLineSegment(sketch, "E325", {"start": v(4.16, -3.1) * mm, "end": v(4.23, -3.17) * mm});
            skLineSegment(sketch, "E326", {"start": v(4.23, -3.17) * mm, "end": v(4.32, -3.23) * mm});
            skLineSegment(sketch, "E327", {"start": v(4.32, -3.23) * mm, "end": v(4.41, -3.28) * mm});
            skLineSegment(sketch, "E328", {"start": v(4.41, -3.28) * mm, "end": v(4.51, -3.33) * mm});
            skLineSegment(sketch, "E329", {"start": v(4.51, -3.33) * mm, "end": v(4.6, -3.37) * mm});
            skLineSegment(sketch, "E330", {"start": v(4.6, -3.37) * mm, "end": v(4.71, -3.4) * mm});
            skLineSegment(sketch, "E331", {"start": v(4.71, -3.4) * mm, "end": v(4.83, -3.45) * mm});
            skLineSegment(sketch, "E332", {"start": v(4.83, -3.45) * mm, "end": v(4.94, -3.48) * mm});
            skLineSegment(sketch, "E333", {"start": v(4.94, -3.48) * mm, "end": v(5.05, -3.5) * mm});
            skLineSegment(sketch, "E334", {"start": v(5.05, -3.5) * mm, "end": v(5.17, -3.53) * mm});
            skLineSegment(sketch, "E335", {"start": v(5.17, -3.53) * mm, "end": v(5.3, -3.55) * mm});
            skLineSegment(sketch, "E336", {"start": v(5.3, -3.55) * mm, "end": v(5.4, -3.57) * mm});
            skLineSegment(sketch, "E337", {"start": v(5.4, -3.57) * mm, "end": v(5.51, -3.58) * mm});
            skLineSegment(sketch, "E338", {"start": v(5.51, -3.58) * mm, "end": v(5.62, -3.59) * mm});
            skLineSegment(sketch, "E339", {"start": v(5.62, -3.59) * mm, "end": v(5.74, -3.6) * mm});
            skLineSegment(sketch, "E340", {"start": v(5.74, -3.6) * mm, "end": v(5.94, -3.6) * mm});
            skLineSegment(sketch, "E341", {"start": v(5.94, -3.6) * mm, "end": v(6.38, -3) * mm});
            skLineSegment(sketch, "E342", {"start": v(6.38, -3) * mm, "end": v(6.3, -2.8) * mm});
            skLineSegment(sketch, "E343", {"start": v(6.3, -2.8) * mm, "end": v(6.27, -2.7) * mm});
            skLineSegment(sketch, "E344", {"start": v(6.27, -2.7) * mm, "end": v(6.22, -2.6) * mm});
            skLineSegment(sketch, "E345", {"start": v(6.22, -2.6) * mm, "end": v(6.18, -2.5) * mm});
            skLineSegment(sketch, "E346", {"start": v(6.18, -2.5) * mm, "end": v(6.13, -2.4) * mm});
            skLineSegment(sketch, "E347", {"start": v(6.13, -2.4) * mm, "end": v(6.07, -2.3) * mm});
            skLineSegment(sketch, "E348", {"start": v(6.07, -2.3) * mm, "end": v(6.01, -2.18) * mm});
            skLineSegment(sketch, "E349", {"start": v(6.01, -2.18) * mm, "end": v(5.95, -2.09) * mm});
            skLineSegment(sketch, "E350", {"start": v(5.95, -2.09) * mm, "end": v(5.89, -2) * mm});
            skLineSegment(sketch, "E351", {"start": v(5.89, -2) * mm, "end": v(5.81, -1.9) * mm});
            skLineSegment(sketch, "E352", {"start": v(5.81, -1.9) * mm, "end": v(5.74, -1.8) * mm});
            skLineSegment(sketch, "E353", {"start": v(5.74, -1.8) * mm, "end": v(5.67, -1.73) * mm});
            skLineSegment(sketch, "E354", {"start": v(5.67, -1.73) * mm, "end": v(5.6, -1.65) * mm});
            skLineSegment(sketch, "E355", {"start": v(5.6, -1.65) * mm, "end": v(5.52, -1.57) * mm});
            skLineSegment(sketch, "E356", {"start": v(5.52, -1.57) * mm, "end": v(5.44, -1.5) * mm});
            skLineSegment(sketch, "E357", {"start": v(5.44, -1.5) * mm, "end": v(5.36, -1.45) * mm});
            skLineSegment(sketch, "E358", {"start": v(5.36, -1.45) * mm, "end": v(4.28, -0.92) * mm});
            skArc(sketch, "E359", {"start": v(4.28, -0.92) * mm, "mid": v(4.48, -0.28) * mm, "end": v(4.7, 0.36) * mm});
            skCircle(sketch, "E360", {"center": v(0, 1.17) * mm, "radius": 1.5 * mm});
            skSolve(sketch);
        }
        {
            var Q0;
            Q0=makeQuery(id+"F0.imprint","IMPRINT",FACE,{"disambiguationData":[TD([[makeQuery(id+"F0.imprint","IMPRINT",EDGE,{"derivedFrom":sQuery(id+"F0.wireOp",EDGE,"E0")}),1.0]])]});
            extrude(context, id + "F1", {"entities" : qUnion([Q0]), "depth" : 5 * mm});
        }
    });
